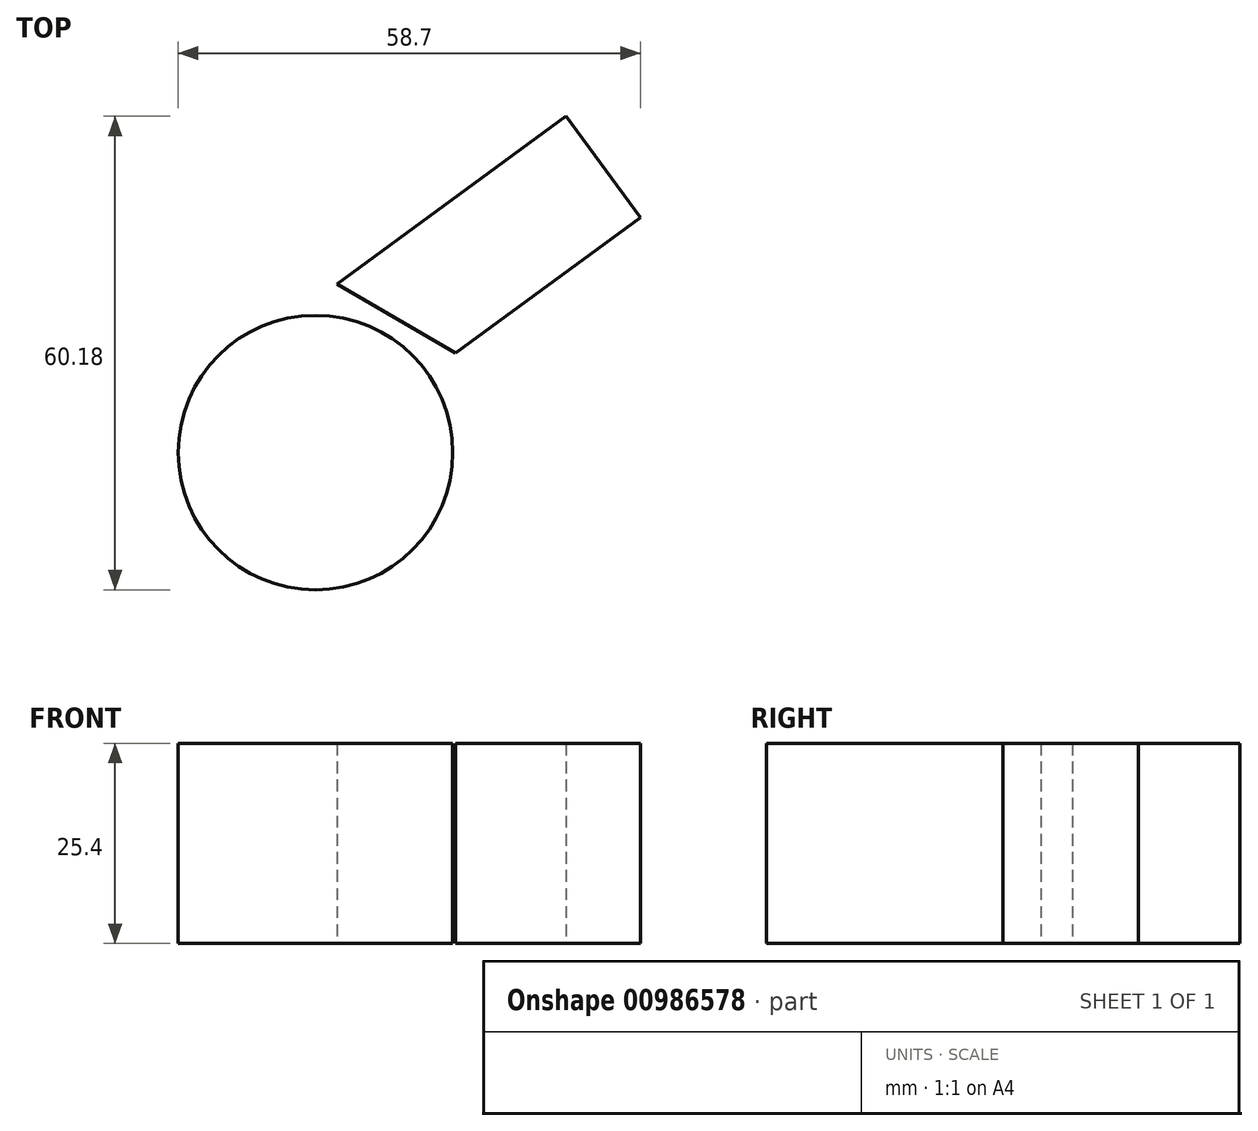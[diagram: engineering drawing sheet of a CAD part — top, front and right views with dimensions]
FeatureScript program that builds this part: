
annotation { "Feature Type Name" : "Feature", "Feature Type Description" : "" }
export const myFeature = defineFeature(function(context is Context, id is Id, definition is map)
    precondition{}
    {
        {
            var Q0;
            Q0=qCreatedBy(makeId("Top.planeOp"),FACE);
            var sketch = newSketch(context, id + "F0", { "sketchPlane" : qUnion([Q0])});
            skCircle(sketch, "E0", {"center": v(0, 0) * mm, "radius": 17.44 * mm});
            skLineSegment(sketch, "E1", {"start": v(2.73, 21.44) * mm, "end": v(31.8, 42.74) * mm});
            skLineSegment(sketch, "E2", {"start": v(31.8, 42.74) * mm, "end": v(41.26, 29.83) * mm});
            skLineSegment(sketch, "E3", {"start": v(41.26, 29.83) * mm, "end": v(17.8, 12.65) * mm});
            skLineSegment(sketch, "E4", {"start": v(17.8, 12.65) * mm, "end": v(2.73, 21.44) * mm});
            skSolve(sketch);
        }
        {
            var Q0;
            Q0 = qSketchRegion(id + "F0", true);
            extrude(context, id + "F1", {"entities" : qUnion([Q0]), "depth" : 25.4 * mm, "offsetDistance" : 25.4 * mm});
        }
    });
